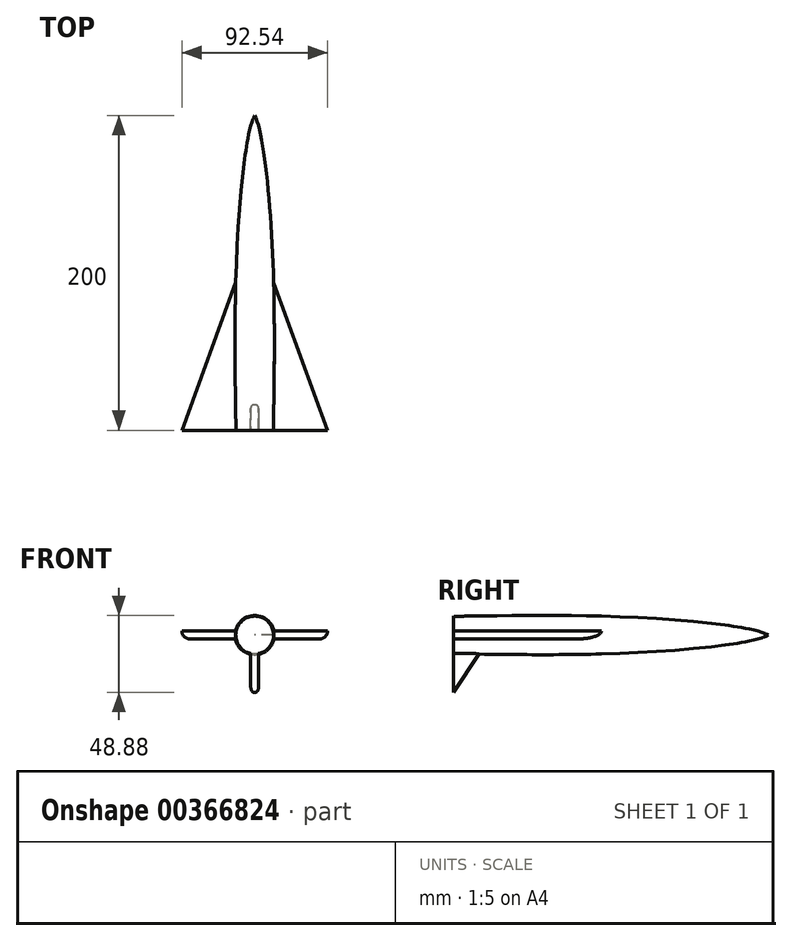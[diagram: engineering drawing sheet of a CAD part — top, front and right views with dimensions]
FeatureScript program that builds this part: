
annotation { "Feature Type Name" : "Feature", "Feature Type Description" : "" }
export const myFeature = defineFeature(function(context is Context, id is Id, definition is map)
    precondition{}
    {
        {
            var Q0;
            Q0=qCreatedBy(makeId("Top.planeOp"),FACE);
            var sketch = newSketch(context, id + "F0", { "sketchPlane" : qUnion([Q0])});
            skLineSegment(sketch, "E0", {"start": v(0, 0) * mm, "end": v(0, 200) * mm});
            skLineSegment(sketch, "E1", {"start": v(0, 0) * mm, "end": v(12, 0) * mm});
            skFitSpline(sketch, "E2", {"points": [v(12, 0) * mm, v(12, 93.94) * mm, v(0, 200) * mm], "startDerivative": vector(-2.07, 34.25) * mm, "endDerivative": vector(-35.86, 64.38) * mm});
            skLineSegment(sketch, "E3", {"start": v(12, 93.94) * mm, "end": v(46.27, 0) * mm});
            skLineSegment(sketch, "E4", {"start": v(46.27, 0) * mm, "end": v(12, 0) * mm});
            skSolve(sketch);
        }
        {
            var Q0;
            Q0=makeQuery(id+"F0.imprint","IMPRINT",FACE,{"disambiguationData":[TD([[makeQuery(id+"F0.imprint","IMPRINT",EDGE,{"derivedFrom":sQuery(id+"F0.wireOp",EDGE,"E0")}),-1.0]])]});
            var Q1;
            Q1=sQuery(id+"F0.wireOp",EDGE,"E0");
            revolve(context, id + "F1", {"entities" : qUnion([Q0]), "axis" : qUnion([Q1]), "revolveType" : RevolveType.FULL});
        }
        {
            var Q0;
            {var subQ0=sQuery(id+"F0.wireOp",EDGE,"E3");Q0=makeQuery(id+"F0.imprint","IMPRINT",FACE,{"disambiguationData":[TD([[makeQuery(id+"F0.imprint","IMPRINT",EDGE,{"derivedFrom":subQ0}),-1.0]])]});}
            extrude(context, id + "F2", {"entities" : qUnion([Q0]), "operationType" : NewBodyOperationType.ADD, "endBound" : BoundingType.SYMMETRIC, "depth" : 5 * mm});
        }
        {
            var Q0;
            Q0=makeQuery(id+"F2.opExtrude","CAP_EDGE",EDGE,{"disambiguationData":[OSD([sQuery(id+"F0.wireOp",EDGE,"E3")])],"isStart":true});
            fillet(context, id + "F3", {"entities" : qUnion([Q0]), "radius" : 5 * mm, "tangentPropagation" : true, "allowEdgeOverflow" : false});
        }
        {
            var Q0;
            Q0=makeQuery(id+"F2.opExtrude","SWEPT_BODY",BODY,{"disambiguationData":[OSD([sQuery(id+"F0.wireOp",EDGE,"E2"),sQuery(id+"F0.wireOp",EDGE,"E3"),sQuery(id+"F0.wireOp",EDGE,"E4")])]});
            var Q1;
            Q1=qCreatedBy(makeId("Right.planeOp"),FACE);
            mirror(context, id + "F4", {"operationType" : NewBodyOperationType.ADD, "entities" : qUnion([Q0]), "mirrorPlane" : qUnion([Q1])});
        }
        {
            var Q0;
            Q0=qCreatedBy(makeId("Right.planeOp"),FACE);
            var sketch = newSketch(context, id + "F5", { "sketchPlane" : qUnion([Q0])});
            skLineSegment(sketch, "E5", {"start": v(0, -6.4) * mm, "end": v(0, -36.4) * mm});
            skLineSegment(sketch, "E6", {"start": v(0, -6.4) * mm, "end": v(20, -6.4) * mm});
            skLineSegment(sketch, "E7", {"start": v(0, -36.4) * mm, "end": v(20, -6.4) * mm});
            skSolve(sketch);
        }
        {
            var Q0;
            Q0=makeQuery(id+"F5.imprint","IMPRINT",FACE,{"disambiguationData":[TD([[makeQuery(id+"F5.imprint","IMPRINT",EDGE,{"derivedFrom":sQuery(id+"F5.wireOp",EDGE,"E5")}),1.0]])]});
            extrude(context, id + "F6", {"entities" : qUnion([Q0]), "operationType" : NewBodyOperationType.ADD, "endBound" : BoundingType.SYMMETRIC, "depth" : 5 * mm});
        }
        {
            var Q0;
            Q0=makeQuery(id+"F6.opExtrude","CAP_EDGE",EDGE,{"disambiguationData":[OSD([sQuery(id+"F5.wireOp",EDGE,"E7")])],"isStart":false});
            fillet(context, id + "F7", {"entities" : qUnion([Q0]), "radius" : 2 * mm, "tangentPropagation" : true, "allowEdgeOverflow" : false});
        }
        {
            var Q0;
            Q0=makeQuery(id+"F6.opExtrude","CAP_EDGE",EDGE,{"disambiguationData":[OSD([sQuery(id+"F5.wireOp",EDGE,"E7")])],"isStart":true});
            fillet(context, id + "F8", {"entities" : qUnion([Q0]), "radius" : 2 * mm, "tangentPropagation" : true, "allowEdgeOverflow" : false});
        }
    });
